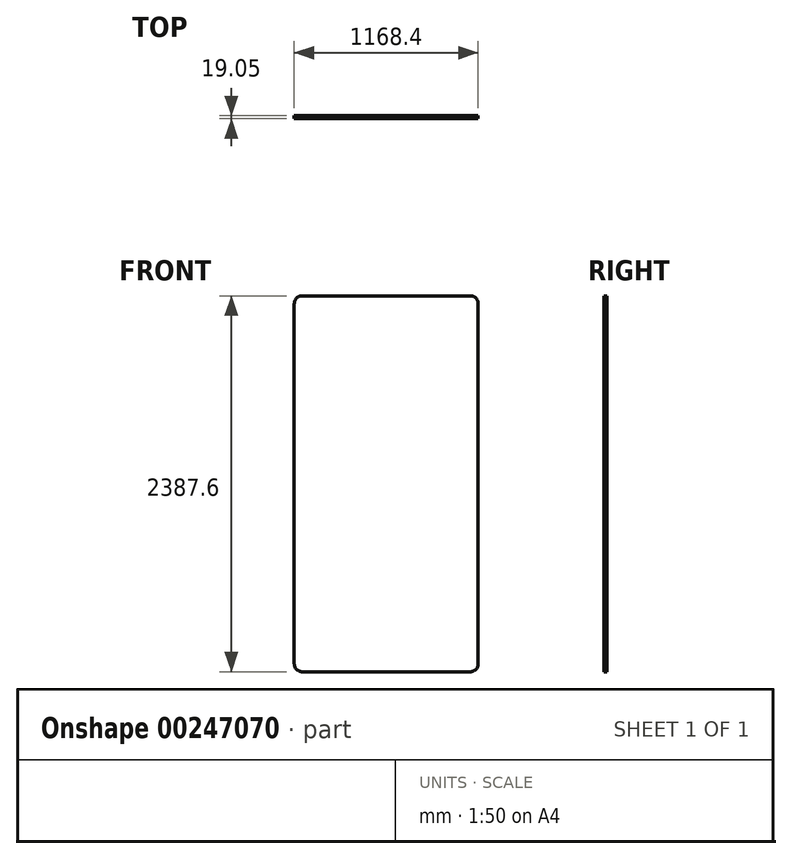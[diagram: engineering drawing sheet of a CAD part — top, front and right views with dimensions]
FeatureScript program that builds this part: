
annotation { "Feature Type Name" : "Feature", "Feature Type Description" : "" }
export const myFeature = defineFeature(function(context is Context, id is Id, definition is map)
    precondition{}
    {
        {
            var Q0;
            Q0=qCreatedBy(makeId("Front.planeOp"),FACE);
            var sketch = newSketch(context, id + "F0", { "sketchPlane" : qUnion([Q0])});
            skLineSegment(sketch, "E0.bottom", {"start": v(584.2, 1193.8) * mm, "end": v(-584.2, 1193.8) * mm});
            skLineSegment(sketch, "E0.top", {"start": v(584.2, -1193.8) * mm, "end": v(-584.2, -1193.8) * mm});
            skLineSegment(sketch, "E0.left", {"start": v(584.2, 1193.8) * mm, "end": v(584.2, -1193.8) * mm});
            skLineSegment(sketch, "E0.right", {"start": v(-584.2, 1193.8) * mm, "end": v(-584.2, -1193.8) * mm});
            skPoint(sketch, "E0.middle", {"position": v(0, 0) * mm});
            skSolve(sketch);
        }
        {
            var Q0;
            Q0=makeQuery(id+"F0.imprint","IMPRINT",FACE,{"disambiguationData":[TD([[makeQuery(id+"F0.imprint","IMPRINT",EDGE,{"derivedFrom":sQuery(id+"F0.wireOp",EDGE,"E0.bottom")}),1.0]])]});
            extrude(context, id + "F1", {"entities" : qUnion([Q0]), "depth" : 19.05 * mm});
        }
        {
            var Q0;
            Q0=makeQuery(id+"F1.opExtrude","SWEPT_EDGE",EDGE,{"disambiguationData":[OSD([sQuery(id+"F0.wireOp",EDGE,"E0.bottom"),sQuery(id+"F0.wireOp",EDGE,"E0.left")])]});
            var Q1;
            Q1=makeQuery(id+"F1.opExtrude","SWEPT_EDGE",EDGE,{"disambiguationData":[OSD([sQuery(id+"F0.wireOp",EDGE,"E0.bottom"),sQuery(id+"F0.wireOp",EDGE,"E0.right")])]});
            var Q2;
            Q2=makeQuery(id+"F1.opExtrude","SWEPT_EDGE",EDGE,{"disambiguationData":[OSD([sQuery(id+"F0.wireOp",EDGE,"E0.top"),sQuery(id+"F0.wireOp",EDGE,"E0.left")])]});
            var Q3;
            Q3=makeQuery(id+"F1.opExtrude","SWEPT_EDGE",EDGE,{"disambiguationData":[OSD([sQuery(id+"F0.wireOp",EDGE,"E0.top"),sQuery(id+"F0.wireOp",EDGE,"E0.right")])]});
            fillet(context, id + "F2", {"entities" : qUnion([Q0, Q1, Q2, Q3]), "radius" : 50.8 * mm, "tangentPropagation" : true, "allowEdgeOverflow" : false});
        }
    });
